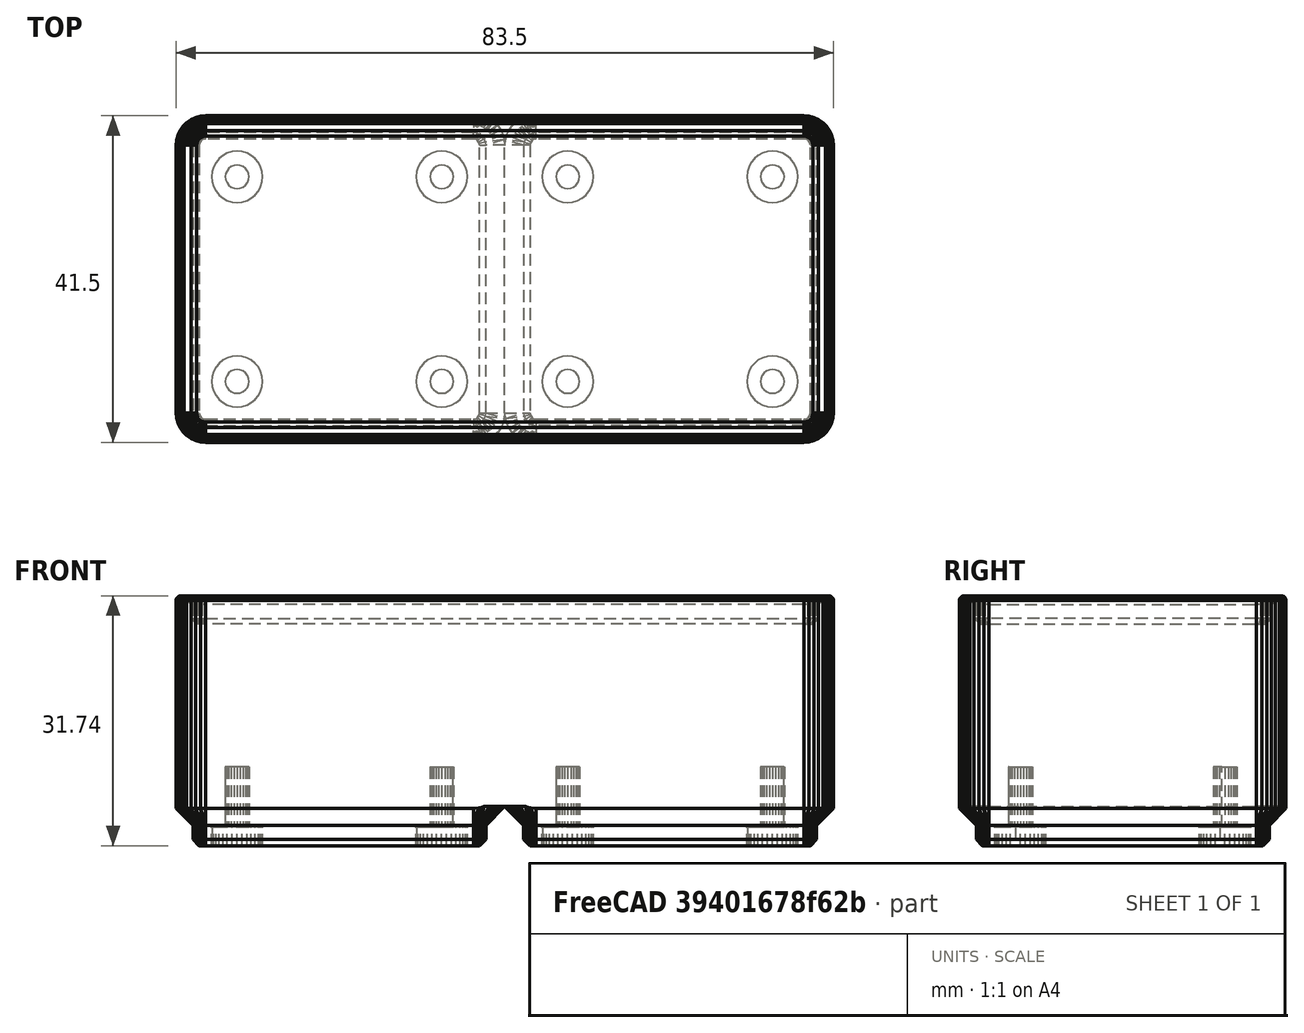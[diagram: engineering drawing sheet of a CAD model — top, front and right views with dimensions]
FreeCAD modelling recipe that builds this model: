
FCSTD DOCUMENT  (FreeCAD 0.20R29410 (Git))
Label: 1x2_plain
License: All rights reserved
LicenseURL: http://en.wikipedia.org/wiki/All_rights_reserved
objects: Part::Feature×2, PartDesign::FeatureBase×1, PartDesign::Body×1, Mesh::Feature×1, Part::Refine×1
note: 5 computed .brp shape members not serialized (recipe doc carries the construction recipe); baked Part::Feature solids carry a one-line shape summary decoded from their .brp

FEATURE [Part::Feature] _x2_Block_1_25in001001_solid  label="_x2_Block_1_25in001001 (Solid)"
  shape: bbox 83.5 x 41.5 x 31.74 mm, 1626 faces (baked)
FEATURE [PartDesign::FeatureBase] BaseFeature
  BaseFeature = -> _x2_Block_1_25in001001_solid
FEATURE [PartDesign::Body] Body
  BaseFeature = -> _x2_Block_1_25in001001_solid
  Group = -> [BaseFeature]
  Origin = -> Origin
  Tip = -> BaseFeature
FEATURE [Mesh::Feature] _x2_Block_1_25in  label="1x2 Block 1.25in"
FEATURE [Part::Feature] _x2_Block_1_25in001
  shape: bbox 83.5 x 41.5 x 31.74 mm, 4368 faces, 0 solids (baked)
FEATURE [Part::Refine] _x2_Block_1_25in001001
  Source = -> _x2_Block_1_25in001
